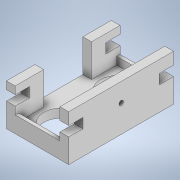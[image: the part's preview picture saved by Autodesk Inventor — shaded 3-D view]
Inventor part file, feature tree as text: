
AUTODESK INVENTOR PART (.ipt)
format: ipt  version: 2020 (Build 240168000, 168)  size: 239,616 bytes
history: native  units: mm
features: extrude x10, sketch x10
ambient origin geometry x8: Origin, YZ Plane, XZ Plane, XY Plane, X Axis, Y Axis, Z Axis, Center Point
bodies: Solid1 (feature_tree)
feature tree (20):
  extrude  "Extrusion1"  Depth=48.0mm
  extrude  "Extrusion2"  Depth=4.0mm
  extrude  "Extrusion3"  Depth=26.0mm
  extrude  "Extrusion4"  Depth=11.0mm
  extrude  "Extrusion5"  Depth=4.0mm TaperAngle=0.0deg
  sketch  "Sketch6"  dims[d9=14.25mm d10=4.0mm d11=0.0mm]
  extrude  "Extrusion6"  Depth=4.0mm
  extrude  "Extrusion7"  Depth=4.0mm
  extrude  "Extrusion8"  Depth=4.0mm
  sketch  "Sketch10"  dims[d19=13.0mm d20=15.0mm d21=0.0mm]
  sketch  "Sketch11"  dims[d22=6.5mm d23=4.5mm d24=11.0mm d25=6.5mm d26=4.5mm d27=11.0mm d28=4.0mm d29=0.0mm d30=5.25mm d31=8.5mm d32=2.0mm d33=0.0mm d34=2.0mm d35=2.0mm d36=0.0mm d37=20.5mm d38=1.5mm d39=1.5mm d40=20.5mm d41=3.5mm d42=0.0mm d43=4.5mm d44=6.5mm d45=11.0mm d46=6.5mm d47=4.5mm d48=11.0mm d49=4.0mm d50=0.0mm d51=4.0mm d52=0.0mm]
  extrude  "Extrusion9"  Depth=15.0mm TaperAngle=0.0deg
  extrude  "Extrusion10"  Depth=4.5mm
  sketch  "Sketch1"  dims[d0=28.5mm d1=48.0mm]
  sketch  "Sketch2"  dims[d2=4.0mm d3=0.0mm d4=16.5mm]
  sketch  "Sketch3"  dims[d5=16.5mm d6=26.0mm]
  sketch  "Sketch4"  dims[d7=11.0mm d8=14.25mm]
  sketch  "Sketch7"  dims[d12=48.0mm d13=4.0mm]
  sketch  "Sketch8"  dims[d14=17.0mm d15=0.0mm d16=4.0mm]
  sketch  "Sketch9"  dims[d17=13.0mm d18=4.0mm]
